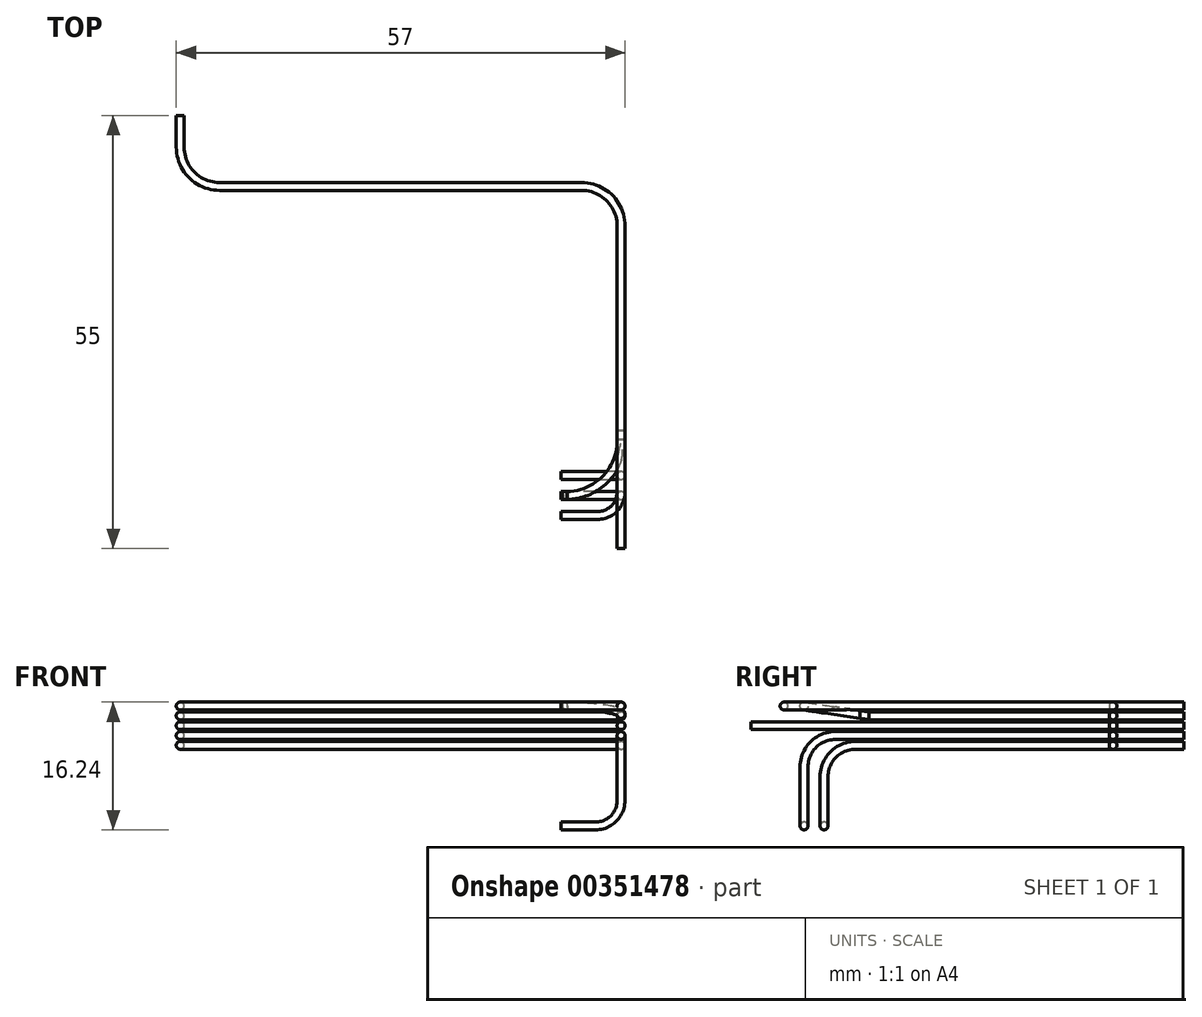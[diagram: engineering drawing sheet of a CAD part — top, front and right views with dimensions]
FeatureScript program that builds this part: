
annotation { "Feature Type Name" : "Feature", "Feature Type Description" : "" }
export const myFeature = defineFeature(function(context is Context, id is Id, definition is map)
    precondition{}
    {
        {
            var Q0;
            Q0=qCreatedBy(makeId("Top.planeOp"),FACE);
            var sketch = newSketch(context, id + "F0", { "sketchPlane" : qUnion([Q0])});
            skLineSegment(sketch, "E0", {"start": v(0, 0) * mm, "end": v(0, 26) * mm});
            skLineSegment(sketch, "E1", {"start": v(-5, 31) * mm, "end": v(-51, 31) * mm});
            skLineSegment(sketch, "E2", {"start": v(-56, 36) * mm, "end": v(-56, 40) * mm});
            skPoint(sketch, "E3.visualSharp", {"position": v(-56, 31) * mm});
            skArc(sketch, "E3.filletArc", {"start": v(-56, 36) * mm, "mid": v(-54.54, 32.46) * mm, "end": v(-51, 31) * mm});
            skPoint(sketch, "E4.visualSharp", {"position": v(0, 31) * mm});
            skArc(sketch, "E4.filletArc", {"start": v(0, 26) * mm, "mid": v(-1.46, 29.54) * mm, "end": v(-5, 31) * mm});
            skSolve(sketch);
        }
        {
            var Q0;
            Q0=qCreatedBy(makeId("Front.planeOp"),FACE);
            var sketch = newSketch(context, id + "F1", { "sketchPlane" : qUnion([Q0])});
            skCircle(sketch, "E5", {"center": v(0, 0) * mm, "radius": 0.5 * mm});
            skCircle(sketch, "E6", {"center": v(0, -1.25) * mm, "radius": 0.5 * mm});
            skCircle(sketch, "E7", {"center": v(0, -2.5) * mm, "radius": 0.5 * mm});
            skCircle(sketch, "E8", {"center": v(0, -3.75) * mm, "radius": 0.5 * mm});
            skCircle(sketch, "E9", {"center": v(0, -5) * mm, "radius": 0.5 * mm});
            skLineSegment(sketch, "E10", {"start": v(0, 0) * mm, "end": v(0, -1.25) * mm, "construction": true});
            skLineSegment(sketch, "E11", {"start": v(0, -1.25) * mm, "end": v(0, -2.5) * mm, "construction": true});
            skLineSegment(sketch, "E12", {"start": v(0, -2.5) * mm, "end": v(0, -3.75) * mm, "construction": true});
            skLineSegment(sketch, "E13", {"start": v(0, -3.75) * mm, "end": v(0, -5) * mm, "construction": true});
            skSolve(sketch);
        }
        {
            var Q0;
            Q0 = qSketchRegion(id + "F1", true);
            var Q1;
            Q1 = qConstructionFilter(qBodyType(qCreatedBy(id + "F0" ,EDGE), BodyType.WIRE), ConstructionObject.NO);
            sweep(context, id + "F2", {"profiles" : qUnion([Q0]), "path" : qUnion([Q1])});
        }
        {
            var Q0;
            Q0=qCreatedBy(makeId("Top.planeOp"),FACE);
            var sketch = newSketch(context, id + "F3", { "sketchPlane" : qUnion([Q0])});
            skLineSegment(sketch, "E14", {"start": v(0, 0) * mm, "end": v(0, -7.8) * mm});
            skLineSegment(sketch, "E15", {"start": v(-3, -10.8) * mm, "end": v(-7.6, -10.8) * mm});
            skPoint(sketch, "E16.visualSharp", {"position": v(0, -10.8) * mm});
            skArc(sketch, "E16.filletArc", {"start": v(-3, -10.8) * mm, "mid": v(-0.88, -9.92) * mm, "end": v(0, -7.8) * mm});
            skPoint(sketch, "E17", {"position": v(-7.6, -8.26) * mm});
            skPoint(sketch, "E18", {"position": v(-5.06, -8.26) * mm});
            skSolve(sketch);
        }
        {
            var Q0;
            Q0=makeQuery(id+"F2.opSweep","CAP_FACE",FACE,{"disambiguationData":[OSD([sQuery(id+"F0.wireOp",VERTEX,"E0.start"),sQuery(id+"F1.wireOp",EDGE,"E5")])],"isStart":true});
            var Q1;
            Q1 = qConstructionFilter(qBodyType(qCreatedBy(id + "F3" ,EDGE), BodyType.WIRE), ConstructionObject.NO);
            sweep(context, id + "F4", {"operationType" : NewBodyOperationType.ADD, "profiles" : qUnion([Q0]), "path" : qUnion([Q1])});
        }
        {
            var Q0;
            Q0=sQuery(id+"F3.wireOp",VERTEX,"E17");
            var Q1;
            Q1=sQuery(id+"F3.wireOp",VERTEX,"E18");
            var Q2;
            Q2=sQuery(id+"F1.wireOp",VERTEX,"E6.center");
            cPlane(context, id + "F5", {"entities" : qUnion([Q0, Q1, Q2]), "cplaneType" : CPlaneType.THREE_POINT, "offset" : 25 * mm, "width" : 150 * mm, "height" : 150 * mm});
        }
        {
            var Q0;
            Q0=qCreatedBy(id+"F5.planeOp",FACE);
            var sketch = newSketch(context, id + "F6", { "sketchPlane" : qUnion([Q0])});
            skPoint(sketch, "E19.0", {"position": v(-7.6, 8.17) * mm});
            skPoint(sketch, "E20.0", {"position": v(-7, 8.17) * mm});
            skLineSegment(sketch, "E21", {"start": v(-7.6, 8.17) * mm, "end": v(-7, 8.17) * mm});
            skPoint(sketch, "E22.0", {"position": v(0, 0) * mm});
            skLineSegment(sketch, "E23", {"start": v(0, 0) * mm, "end": v(0, 1.17) * mm});
            skArc(sketch, "E24", {"start": v(0, 1.17) * mm, "mid": v(-2.05, 6.12) * mm, "end": v(-7, 8.17) * mm});
            skSolve(sketch);
        }
        {
            var Q0;
            Q0=makeQuery(id+"F1.imprint","IMPRINT",FACE,{"disambiguationData":[TD([[makeQuery(id+"F1.imprint","IMPRINT",EDGE,{"derivedFrom":sQuery(id+"F1.wireOp",EDGE,"E6")}),1.0]])]});
            var Q1;
            Q1 = qConstructionFilter(qBodyType(qCreatedBy(id + "F6" ,EDGE), BodyType.WIRE), ConstructionObject.NO);
            sweep(context, id + "F7", {"operationType" : NewBodyOperationType.ADD, "profiles" : qUnion([Q0]), "path" : qUnion([Q1])});
        }
        {
            var Q0;
            Q0=makeQuery(id+"F1.imprint","IMPRINT",FACE,{"disambiguationData":[TD([[makeQuery(id+"F1.imprint","IMPRINT",EDGE,{"derivedFrom":sQuery(id+"F1.wireOp",EDGE,"E7")}),1.0]])]});
            extrude(context, id + "F8", {"entities" : qUnion([Q0]), "operationType" : NewBodyOperationType.ADD, "depth" : 15 * mm});
        }
        {
            var Q0;
            Q0=qCreatedBy(makeId("Right.planeOp"),FACE);
            var sketch = newSketch(context, id + "F9", { "sketchPlane" : qUnion([Q0])});
            skPoint(sketch, "E25.0", {"position": v(-8.26, 0) * mm});
            skPoint(sketch, "E26.0", {"position": v(0, -3.75) * mm});
            skPoint(sketch, "E27.0", {"position": v(0, -5) * mm});
            skLineSegment(sketch, "E28", {"start": v(0, -3.75) * mm, "end": v(-4.26, -3.75) * mm});
            skLineSegment(sketch, "E29", {"start": v(-8.26, -7.75) * mm, "end": v(-8.26, -12) * mm});
            skLineSegment(sketch, "E30", {"start": v(0, -5) * mm, "end": v(-1.72, -5) * mm});
            skLineSegment(sketch, "E31", {"start": v(-5.72, -9) * mm, "end": v(-5.72, -12) * mm});
            skPoint(sketch, "E32.visualSharp", {"position": v(-8.26, -3.75) * mm});
            skArc(sketch, "E32.filletArc", {"start": v(-4.26, -3.75) * mm, "mid": v(-7.09, -4.92) * mm, "end": v(-8.26, -7.75) * mm});
            skPoint(sketch, "E33.visualSharp", {"position": v(-5.72, -5) * mm});
            skArc(sketch, "E33.filletArc", {"start": v(-1.72, -5) * mm, "mid": v(-4.55, -6.17) * mm, "end": v(-5.72, -9) * mm});
            skSolve(sketch);
        }
        {
            var Q0;
            Q0=makeQuery(id+"F1.imprint","IMPRINT",FACE,{"disambiguationData":[TD([[makeQuery(id+"F1.imprint","IMPRINT",EDGE,{"derivedFrom":sQuery(id+"F1.wireOp",EDGE,"E8")}),1.0]])]});
            var Q1;
            Q1=sQuery(id+"F9.wireOp",EDGE,"E28");
            var Q2;
            Q2=sQuery(id+"F9.wireOp",EDGE,"E29");
            var Q3;
            Q3=sQuery(id+"F9.wireOp",EDGE,"E32.filletArc");
            sweep(context, id + "F10", {"operationType" : NewBodyOperationType.ADD, "profiles" : qUnion([Q0]), "path" : qUnion([Q1, Q2, Q3])});
        }
        {
            var Q0;
            Q0=makeQuery(id+"F1.imprint","IMPRINT",FACE,{"disambiguationData":[TD([[makeQuery(id+"F1.imprint","IMPRINT",EDGE,{"derivedFrom":sQuery(id+"F1.wireOp",EDGE,"E9")}),1.0]])]});
            var Q1;
            Q1=sQuery(id+"F9.wireOp",EDGE,"E30");
            var Q2;
            Q2=sQuery(id+"F9.wireOp",EDGE,"E33.filletArc");
            var Q3;
            Q3=sQuery(id+"F9.wireOp",EDGE,"E31");
            sweep(context, id + "F11", {"operationType" : NewBodyOperationType.ADD, "profiles" : qUnion([Q0]), "path" : qUnion([Q1, Q2, Q3])});
        }
        {
            var Q0;
            Q0=qCreatedBy(makeId("Front.planeOp"),FACE);
            var Q1;
            Q1=sQuery(id+"F9.wireOp",VERTEX,"E29.end");
            cPlane(context, id + "F12", {"entities" : qUnion([Q0, Q1]), "cplaneType" : CPlaneType.PLANE_POINT, "offset" : 25 * mm, "width" : 150 * mm, "height" : 150 * mm});
        }
        {
            var Q0;
            Q0=qCreatedBy(id+"F12.planeOp",FACE);
            var sketch = newSketch(context, id + "F13", { "sketchPlane" : qUnion([Q0])});
            skPoint(sketch, "E34.0", {"position": v(0, -12) * mm});
            skArc(sketch, "E35", {"start": v(-3.24, -15.24) * mm, "mid": v(-0.95, -14.3) * mm, "end": v(0, -12) * mm});
            skLineSegment(sketch, "E36", {"start": v(0, -12) * mm, "end": v(0, -5.85) * mm, "construction": true});
            skPoint(sketch, "E37.0", {"position": v(-7.6, 0) * mm});
            skLineSegment(sketch, "E38", {"start": v(-3.24, -15.24) * mm, "end": v(-7.6, -15.24) * mm});
            skSolve(sketch);
        }
        {
            var Q0;
            Q0=makeQuery(id+"F11.opSweep","CAP_FACE",FACE,{"disambiguationData":[OSD([sQuery(id+"F1.wireOp",EDGE,"E9"),sQuery(id+"F9.wireOp",VERTEX,"E31.end")])],"isStart":false});
            var Q1;
            Q1=makeQuery(id+"F10.opSweep","CAP_FACE",FACE,{"disambiguationData":[OSD([sQuery(id+"F1.wireOp",EDGE,"E8"),sQuery(id+"F9.wireOp",VERTEX,"E29.end")])],"isStart":false});
            var Q2;
            Q2 = qConstructionFilter(qBodyType(qCreatedBy(id + "F13" ,EDGE), BodyType.WIRE), ConstructionObject.NO);
            sweep(context, id + "F14", {"operationType" : NewBodyOperationType.ADD, "profiles" : qUnion([Q0, Q1]), "path" : qUnion([Q2])});
        }
    });
